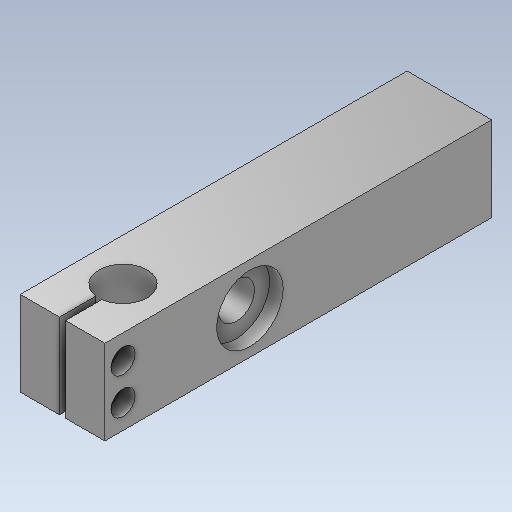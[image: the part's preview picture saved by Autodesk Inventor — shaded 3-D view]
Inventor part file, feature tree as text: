
AUTODESK INVENTOR PART (.ipt)
format: ipt  version: 2020 (Build 240168000, 168)  size: 277,504 bytes
history: native  units: in
note: dims shown in document units (in); Inventor stores cm internally (conversion verified against a paired STEP export)
features: sketch x9, extrude x8, reference x4, other x3
ambient origin geometry x8: Origin, YZ Plane, XZ Plane, XY Plane, X Axis, Y Axis, Z Axis, Center Point
bodies: Solid1 (feature_tree)
feature tree (24):
  extrude  "Extrusion1"  Depth=0.375in
  extrude  "Extrusion2"  Depth=1.75in
  sketch  "Sketch3"  dims[d4=1.5in d5=0.0in d6=6.5in d7=0.0in]
  extrude  "Extrusion3"  Depth=6.5in TaperAngle=0.0deg
  extrude  "Extrusion4"  Depth=0.2812in TaperAngle=0.0deg
  extrude  "Extrusion5"  Depth=0.75in
  extrude  "Extrusion6"  Depth=1.0in
  extrude  "Extrusion7"  Depth=2.0in TaperAngle=0.0deg
  extrude  "Extrusion8"  Depth=0.8125in
  sketch  "Sketch1"  dims[d0=0.375in d1=0.375in]
  reference  "Reference1"
  reference  "Reference2"
  reference  "Reference3"
  reference  "Reference4"
  sketch  "Sketch2"  dims[d2=1.75in d3=1.75in]
  sketch  "Sketch4"  dims[d8=1.375in d9=0.2812in d10=0.0in]
  sketch  "Sketch5"  dims[d11=5.0in d12=0.75in]
  sketch  "Sketch6"  dims[d13=2.0in d14=0.0in d15=1.0in]
  sketch  "Sketch7"  dims[d16=1.25in d17=2.0in d18=0.0in]
  sketch  "Sketch8"  dims[d19=0.125in d20=0.8125in]
  sketch  "Sketch9"  dims[d21=1.0in d22=2.0in d23=0.0in d24=0.5in d25=0.375in d26=0.5in d27=0.5in d28=0.5in d29=0.3125in d30=0.0in d31=0.3125in d32=0.3125in d33=1.5in d34=0.0in]
  other  "<userpath>\Desktop\PnP Machine\PnP Machine.iam"
  other  "PnP Machine.iam"
  other  "Corner Stands:1"
